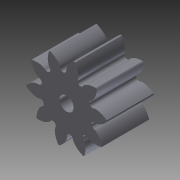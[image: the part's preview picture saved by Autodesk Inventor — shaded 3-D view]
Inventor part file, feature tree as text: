
AUTODESK INVENTOR PART (.ipt)
format: ipt  version: 2013 (Build 170138000, 138)  size: 356,864 bytes
history: native  units: in
note: dims shown in document units (in); Inventor stores cm internally (conversion verified against a paired STEP export)
features: extrude x1, sketch x1
ambient origin geometry x8: Origin, YZ Plane, XZ Plane, XY Plane, X Axis, Y Axis, Z Axis, Center Point
bodies: Solid1 (feature_tree)
feature tree (2):
  extrude  "Extrusion1"  [1 undecoded]
  sketch  "Sketch1"  dims[d0=0.118in d1=0.0in]
note: 1 required parameter value undecoded (feature->parameter linkage not recoverable at this tier; creation-order binding heuristic only, values carry confidence <= 0.55)
